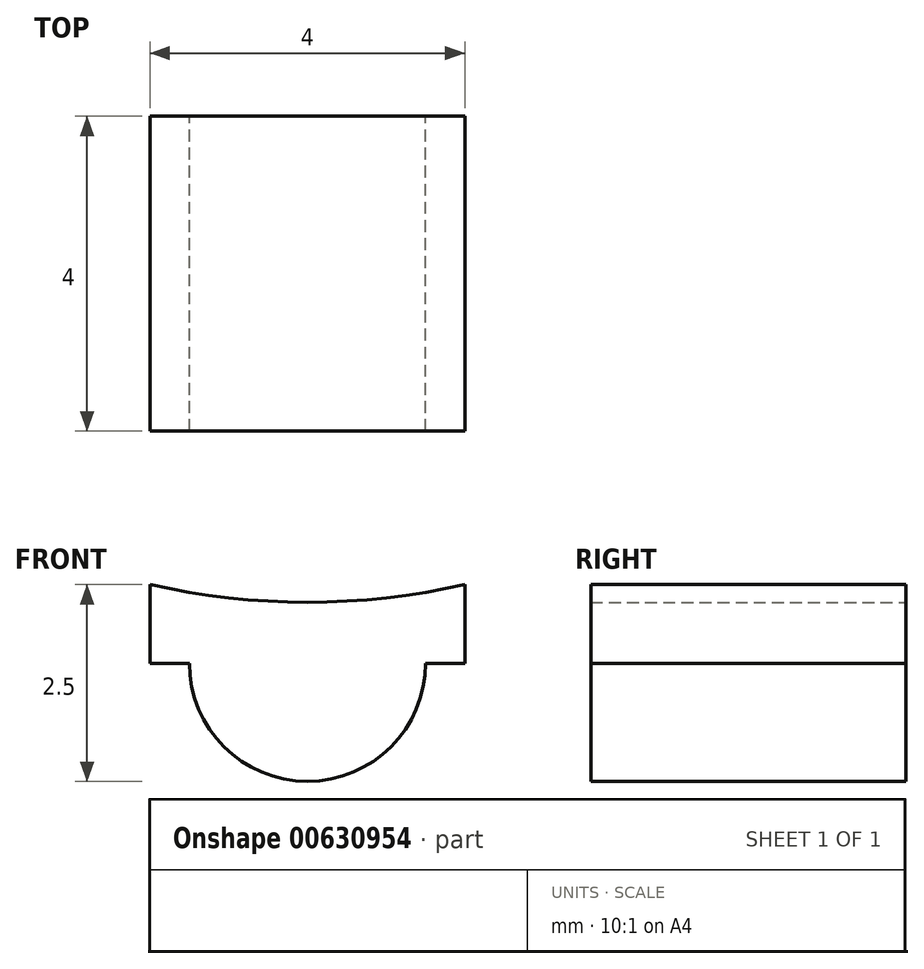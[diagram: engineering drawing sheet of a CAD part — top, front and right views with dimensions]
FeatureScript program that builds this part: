
annotation { "Feature Type Name" : "Feature", "Feature Type Description" : "" }
export const myFeature = defineFeature(function(context is Context, id is Id, definition is map)
    precondition{}
    {
        {
            var Q0;
            Q0=qCreatedBy(makeId("Front.planeOp"),FACE);
            var sketch = newSketch(context, id + "F0", { "sketchPlane" : qUnion([Q0])});
            skCircle(sketch, "E0", {"center": v(0, 0) * mm, "radius": 1.5 * mm});
            skSolve(sketch);
        }
        {
            var Q0;
            Q0=qSketchRegion(id+"F0",true);
            extrude(context, id + "F1", {"entities" : qUnion([Q0]), "depth" : 4 * mm, "offsetDistance" : 25 * mm});
        }
        {
            var Q0;
            Q0=qCreatedBy(makeId("Top.planeOp"),FACE);
            var sketch = newSketch(context, id + "F2", { "sketchPlane" : qUnion([Q0])});
            skLineSegment(sketch, "E1.bottom", {"start": v(0, 0) * mm, "end": v(2, 0) * mm});
            skLineSegment(sketch, "E1.left", {"start": v(0, 0) * mm, "end": v(0, -3) * mm});
            skLineSegment(sketch, "E2", {"start": v(0, 0) * mm, "end": v(0, -7.8) * mm, "construction": true});
            skLineSegment(sketch, "E3.0", {"start": v(1.5, -4) * mm, "end": v(-1.5, -4) * mm, "construction": true});
            skPoint(sketch, "E4", {"position": v(0, -4) * mm});
            skLineSegment(sketch, "E5", {"start": v(0, -4) * mm, "end": v(2, -4) * mm});
            skLineSegment(sketch, "E6", {"start": v(2, 0) * mm, "end": v(2, -4) * mm});
            skLineSegment(sketch, "E7", {"start": v(0, -4) * mm, "end": v(0, 0.08) * mm});
            skPoint(sketch, "E7.endSnap0", {"position": v(0, -3.9) * mm});
            skLineSegment(sketch, "E8.MirrorCS", {"start": v(0, -4) * mm, "end": v(-2, -4) * mm});
            skLineSegment(sketch, "E9.MirrorCS", {"start": v(-2, 0) * mm, "end": v(-2, -4) * mm});
            skLineSegment(sketch, "E10.MirrorCS", {"start": v(0, 0) * mm, "end": v(-2, 0) * mm});
            skSolve(sketch);
        }
        {
            var Q0;
            Q0=qSketchRegion(id+"F2",true);
            extrude(context, id + "F3", {"entities" : qUnion([Q0]), "operationType" : NewBodyOperationType.ADD, "depth" : 1 * mm, "offsetDistance" : 25 * mm});
        }
        {
            var Q0;
            {var subQ1=sQuery(id+"F2.wireOp",EDGE,"E10.MirrorCS");var subQ2=sQuery(id+"F2.wireOp",EDGE,"E1.bottom");var subQ3=sQuery(id+"F2.wireOp",EDGE,"E8.MirrorCS");var subQ4=sQuery(id+"F2.wireOp",EDGE,"E5");var subQ5=sQuery(id+"F2.wireOp",EDGE,"E6");Q0=makeQuery(id+"F3.boolean.opBoolean","SPLIT",FACE,{"disambiguationData":[TD([makeQuery(id+"F3.opExtrude","SWEPT_FACE",FACE,{"disambiguationData":[OSD([subQ5])]})])],"derivedFrom":makeQuery(id+"F3.opExtrude","CAP_FACE",FACE,{"disambiguationData":[OSD([subQ2,subQ4,subQ5,subQ3,sQuery(id+"F2.wireOp",EDGE,"E9.MirrorCS"),subQ1])],"isStart":false})});}
            var sketch = newSketch(context, id + "F4", { "sketchPlane" : qUnion([Q0])});
            skLineSegment(sketch, "E11.bottom", {"start": v(-4.25, 3.62) * mm, "end": v(5.8, 3.62) * mm});
            skLineSegment(sketch, "E11.top", {"start": v(-4.25, -6.13) * mm, "end": v(5.8, -6.13) * mm});
            skLineSegment(sketch, "E11.left", {"start": v(-4.25, 3.62) * mm, "end": v(-4.25, -6.13) * mm});
            skLineSegment(sketch, "E11.right", {"start": v(5.8, 3.62) * mm, "end": v(5.8, -6.13) * mm});
            skSolve(sketch);
        }
        {
            var Q0;
            Q0 = qSketchRegion(id + "F4", true);
            extrude(context, id + "F5", {"entities" : qUnion([Q0]), "operationType" : NewBodyOperationType.REMOVE, "depth" : 25 * mm, "offsetDistance" : 25 * mm});
        }
        {
            var Q0;
            Q0=makeQuery(id+"F3.boolean.opBoolean","MERGE",FACE,{"derivedFrom":[makeQuery(id+"F1.opExtrude","CAP_FACE",FACE,{"disambiguationData":[OSD([sQuery(id+"F0.wireOp",EDGE,"E0")])],"isStart":true}),makeQuery(id+"F3.opExtrude","SWEPT_FACE",FACE,{"disambiguationData":[OSD([sQuery(id+"F2.wireOp",EDGE,"E1.bottom"),sQuery(id+"F2.wireOp",EDGE,"E10.MirrorCS")])]})]});
            var sketch = newSketch(context, id + "F6", { "sketchPlane" : qUnion([Q0])});
            skLineSegment(sketch, "E12.0", {"start": v(2, 1) * mm, "end": v(-2, 1) * mm, "construction": true});
            skLineSegment(sketch, "E13.0", {"start": v(-2, 1) * mm, "end": v(-2, 0) * mm, "construction": true});
            skLineSegment(sketch, "E14.0", {"start": v(2, 1) * mm, "end": v(2, 0) * mm, "construction": true});
            skArc(sketch, "E15", {"start": v(-2, 1) * mm, "mid": v(0, 0.77) * mm, "end": v(2, 1) * mm});
            skLineSegment(sketch, "E16", {"start": v(2, 1) * mm, "end": v(2, 1.92) * mm});
            skLineSegment(sketch, "E17", {"start": v(2, 1.92) * mm, "end": v(-2.08, 1.92) * mm});
            skLineSegment(sketch, "E18", {"start": v(-2.08, 1.92) * mm, "end": v(-2, 1) * mm});
            skSolve(sketch);
        }
        {
            var Q0;
            Q0 = qSketchRegion(id + "F6", true);
            extrude(context, id + "F7", {"entities" : qUnion([Q0]), "operationType" : NewBodyOperationType.REMOVE, "oppositeDirection" : true, "depth" : 25 * mm, "offsetDistance" : 25 * mm});
        }
    });
